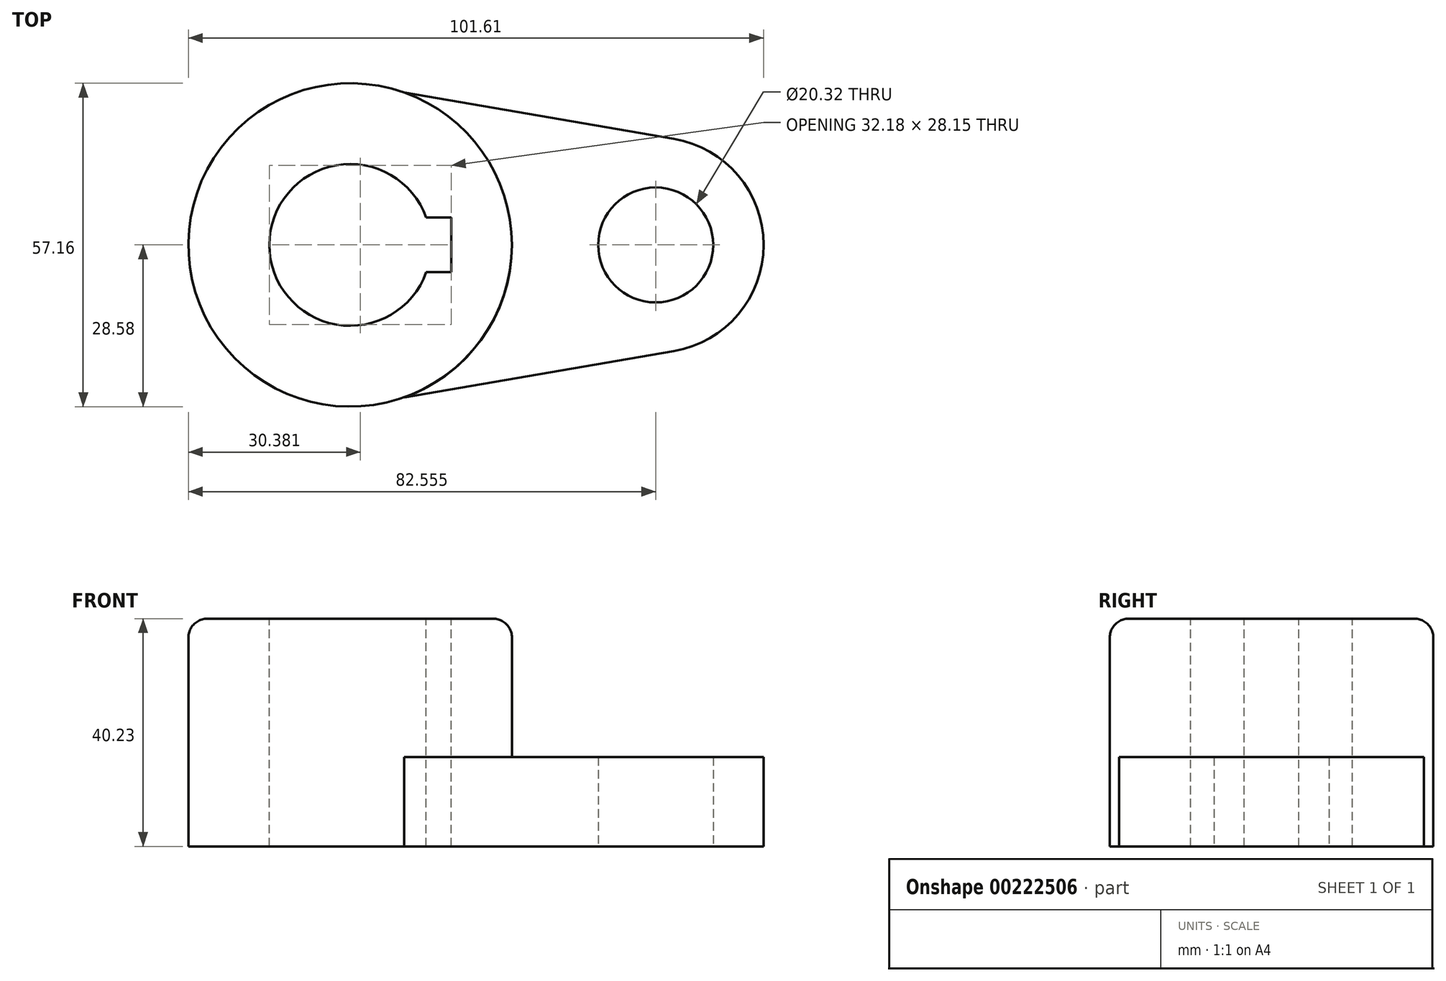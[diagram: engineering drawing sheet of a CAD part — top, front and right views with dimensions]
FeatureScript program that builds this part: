
annotation { "Feature Type Name" : "Feature", "Feature Type Description" : "" }
export const myFeature = defineFeature(function(context is Context, id is Id, definition is map)
    precondition{}
    {
        {
            var Q0;
            Q0=qCreatedBy(makeId("Top.planeOp"),FACE);
            var sketch = newSketch(context, id + "F0", { "sketchPlane" : qUnion([Q0])});
            skCircle(sketch, "E0", {"center": v(0, 0) * mm, "radius": 28.58 * mm});
            skLineSegment(sketch, "E1", {"start": v(9.51, 26.95) * mm, "end": v(57.2, 18.78) * mm});
            skLineSegment(sketch, "E2.MirrorCS", {"start": v(9.51, -26.95) * mm, "end": v(57.2, -18.78) * mm});
            skCircle(sketch, "E3", {"center": v(53.98, 0) * mm, "radius": 10.16 * mm});
            skLineSegment(sketch, "E4", {"start": v(64.13, 0) * mm, "end": v(149.07, 0) * mm, "construction": true});
            skCircle(sketch, "E5", {"center": v(53.98, 0) * mm, "radius": 19.05 * mm});
            skPoint(sketch, "E6.orphan", {"position": v(0, -28.57) * mm});
            skPoint(sketch, "E7.orphan", {"position": v(0, 28.57) * mm});
            skSolve(sketch);
        }
        {
            var Q0;
            {var subQ0=sQuery(id+"F0.wireOp",EDGE,"E0");var subQ1=makeQuery(id+"F0.imprint","INTERSECT",VERTEX,{"derivedFrom":[subQ0,sQuery(id+"F0.wireOp",EDGE,"E1")]});Q0=makeQuery(id+"F0.imprint","IMPRINT",FACE,{"disambiguationData":[TD([[makeQuery(id+"F0.imprint","IMPRINT",EDGE,{"disambiguationData":[TD([[subQ1,-1.0]])],"derivedFrom":subQ0}),1.0]])]});}
            extrude(context, id + "F1", {"entities" : qUnion([Q0]), "depth" : 40.23 * mm});
        }
        {
            var Q0;
            Q0=qCreatedBy(makeId("Top.planeOp"),FACE);
            var sketch = newSketch(context, id + "F2", { "sketchPlane" : qUnion([Q0])});
            skCircle(sketch, "E8.0", {"center": v(53.98, 0) * mm, "radius": 19.05 * mm});
            skCircle(sketch, "E8.1", {"center": v(53.98, 0) * mm, "radius": 10.16 * mm});
            skLineSegment(sketch, "E8.3", {"start": v(9.51, -26.95) * mm, "end": v(57.2, -18.78) * mm});
            skLineSegment(sketch, "E8.4", {"start": v(9.51, 26.95) * mm, "end": v(57.2, 18.78) * mm});
            skSolve(sketch);
        }
        {
            var Q0;
            Q0 = qSketchRegion(id + "F2", true);
            var Q1;
            {var subQ0=sQuery(id+"F0.wireOp",EDGE,"E1");Q1=makeQuery(id+"F0.imprint","IMPRINT",FACE,{"disambiguationData":[TD([[makeQuery(id+"F0.imprint","IMPRINT",EDGE,{"derivedFrom":subQ0}),-1.0]])]});}
            extrude(context, id + "F3", {"entities" : qUnion([Q0, Q1]), "operationType" : NewBodyOperationType.ADD, "depth" : 15.77 * mm});
        }
        {
            var Q0;
            Q0=makeQuery(id+"F1.opExtrude","CAP_FACE",FACE,{"disambiguationData":[OSD([sQuery(id+"F0.wireOp",EDGE,"E0")])],"isStart":false});
            var sketch = newSketch(context, id + "F4", { "sketchPlane" : qUnion([Q0])});
            skArc(sketch, "E9", {"start": v(13.45, 4.83) * mm, "mid": v(-14.29, 0) * mm, "end": v(13.45, -4.83) * mm});
            skLineSegment(sketch, "E10", {"start": v(13.45, 4.83) * mm, "end": v(17.89, 4.83) * mm});
            skLineSegment(sketch, "E11", {"start": v(17.89, 4.83) * mm, "end": v(17.89, -4.83) * mm});
            skLineSegment(sketch, "E12", {"start": v(0, 0) * mm, "end": v(17.89, 0) * mm, "construction": true});
            skLineSegment(sketch, "E13.MirrorCS", {"start": v(13.45, -4.83) * mm, "end": v(17.89, -4.83) * mm});
            skSolve(sketch);
        }
        {
            var Q0;
            Q0 = qSketchRegion(id + "F4", true);
            extrude(context, id + "F5", {"entities" : qUnion([Q0]), "operationType" : NewBodyOperationType.REMOVE, "endBound" : BoundingType.THROUGH_ALL, "oppositeDirection" : true, "depth" : 25.4 * mm});
        }
        {
            var Q0;
            Q0=makeQuery(id+"F1.opExtrude","CAP_EDGE",EDGE,{"disambiguationData":[OSD([sQuery(id+"F0.wireOp",EDGE,"E0")])],"isStart":false});
            fillet(context, id + "F6", {"entities" : qUnion([Q0]), "radius" : 3.3 * mm, "tangentPropagation" : true, "allowEdgeOverflow" : false});
        }
    });
